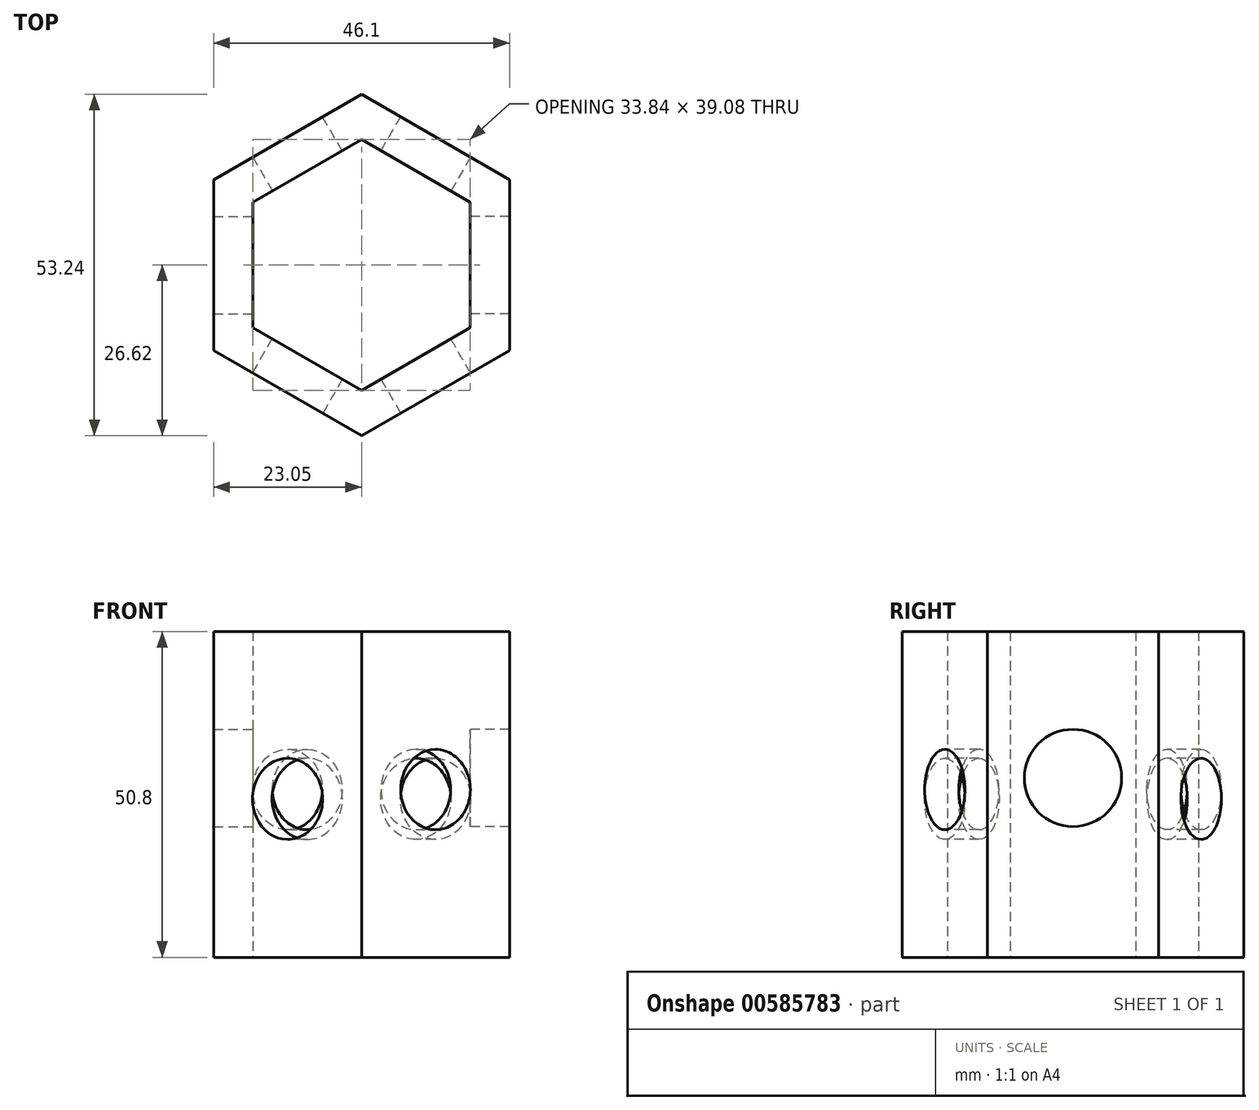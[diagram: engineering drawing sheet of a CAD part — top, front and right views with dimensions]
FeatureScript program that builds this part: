
annotation { "Feature Type Name" : "Feature", "Feature Type Description" : "" }
export const myFeature = defineFeature(function(context is Context, id is Id, definition is map)
    precondition{}
    {
        {
            var Q0;
            Q0=qCreatedBy(makeId("Top.planeOp"),FACE);
            var sketch = newSketch(context, id + "F0", { "sketchPlane" : qUnion([Q0])});
            skCircle(sketch, "E0.cCircle", {"center": v(0, 0) * mm, "radius": 23.05 * mm, "construction": true});
            skLineSegment(sketch, "E0.0", {"start": v(-23.05, -13.3) * mm, "end": v(-23.05, 13.3) * mm});
            skLineSegment(sketch, "E0.1", {"start": v(-23.05, 13.3) * mm, "end": v(0, 26.62) * mm});
            skLineSegment(sketch, "E0.2", {"start": v(0, 26.62) * mm, "end": v(23.05, 13.3) * mm});
            skLineSegment(sketch, "E0.3", {"start": v(23.05, 13.3) * mm, "end": v(23.05, -13.3) * mm});
            skLineSegment(sketch, "E0.4", {"start": v(23.05, -13.3) * mm, "end": v(0, -26.62) * mm});
            skLineSegment(sketch, "E0.5", {"start": v(0, -26.62) * mm, "end": v(-23.05, -13.3) * mm});
            skPoint(sketch, "E0.0.midPoint", {"position": v(-23.05, 0) * mm});
            skCircle(sketch, "E1.cCircle", {"center": v(0, 0) * mm, "radius": 16.92 * mm, "construction": true});
            skLineSegment(sketch, "E1.0", {"start": v(-16.92, -9.77) * mm, "end": v(-16.92, 9.77) * mm});
            skLineSegment(sketch, "E1.1", {"start": v(-16.92, 9.77) * mm, "end": v(0, 19.54) * mm});
            skLineSegment(sketch, "E1.2", {"start": v(0, 19.54) * mm, "end": v(16.92, 9.77) * mm});
            skLineSegment(sketch, "E1.3", {"start": v(16.92, 9.77) * mm, "end": v(16.92, -9.77) * mm});
            skLineSegment(sketch, "E1.4", {"start": v(16.92, -9.77) * mm, "end": v(0, -19.54) * mm});
            skLineSegment(sketch, "E1.5", {"start": v(0, -19.54) * mm, "end": v(-16.92, -9.77) * mm});
            skPoint(sketch, "E1.0.midPoint", {"position": v(-16.92, 0) * mm});
            skSolve(sketch);
        }
        {
            var Q0;
            Q0 = qSketchRegion(id + "F0", true);
            extrude(context, id + "F1", {"entities" : qUnion([Q0]), "depth" : 50.8 * mm, "offsetDistance" : 25.4 * mm});
        }
        {
            var Q0;
            Q0=qCreatedBy(makeId("Right.planeOp"),FACE);
            var sketch = newSketch(context, id + "F2", { "sketchPlane" : qUnion([Q0])});
            skCircle(sketch, "E2", {"center": v(0, 27.95) * mm, "radius": 7.58 * mm});
            skSolve(sketch);
        }
        {
            var Q0;
            Q0 = qSketchRegion(id + "F2", true);
            extrude(context, id + "F3", {"entities" : qUnion([Q0]), "operationType" : NewBodyOperationType.REMOVE, "depth" : 38.1 * mm, "offsetDistance" : 25.4 * mm});
        }
        {
            var Q0;
            Q0 = qSketchRegion(id + "F2", true);
            extrude(context, id + "F4", {"entities" : qUnion([Q0]), "operationType" : NewBodyOperationType.REMOVE, "oppositeDirection" : true, "depth" : 38.1 * mm, "offsetDistance" : 25.4 * mm});
        }
        {
            var Q0;
            Q0=makeQuery(id+"F1.opExtrude","SWEPT_FACE",FACE,{"disambiguationData":[OSD([sQuery(id+"F0.wireOp",EDGE,"E0.5")])]});
            var sketch = newSketch(context, id + "F5", { "sketchPlane" : qUnion([Q0])});
            skCircle(sketch, "E3", {"center": v(0, 24.7) * mm, "radius": 6.32 * mm});
            skSolve(sketch);
        }
        {
            var Q0;
            Q0=makeQuery(id+"F5.imprint","IMPRINT",FACE,{"disambiguationData":[TD([[makeQuery(id+"F5.imprint","IMPRINT",EDGE,{"derivedFrom":sQuery(id+"F5.wireOp",EDGE,"E3")}),1.0]])]});
            extrude(context, id + "F6", {"entities" : qUnion([Q0]), "operationType" : NewBodyOperationType.REMOVE, "oppositeDirection" : true, "depth" : 76.2 * mm, "offsetDistance" : 25.4 * mm});
        }
        {
            var Q0;
            Q0=makeQuery(id+"F1.opExtrude","SWEPT_FACE",FACE,{"disambiguationData":[OSD([sQuery(id+"F0.wireOp",EDGE,"E0.4")])]});
            var sketch = newSketch(context, id + "F7", { "sketchPlane" : qUnion([Q0])});
            skCircle(sketch, "E4", {"center": v(0, 26.15) * mm, "radius": 6.26 * mm});
            skSolve(sketch);
        }
        {
            var Q0;
            Q0=makeQuery(id+"F7.imprint","IMPRINT",FACE,{"disambiguationData":[TD([[makeQuery(id+"F7.imprint","IMPRINT",EDGE,{"derivedFrom":sQuery(id+"F7.wireOp",EDGE,"E4")}),1.0]])]});
            extrude(context, id + "F8", {"entities" : qUnion([Q0]), "operationType" : NewBodyOperationType.REMOVE, "oppositeDirection" : true, "depth" : 50.8 * mm, "offsetDistance" : 25.4 * mm});
        }
    });
